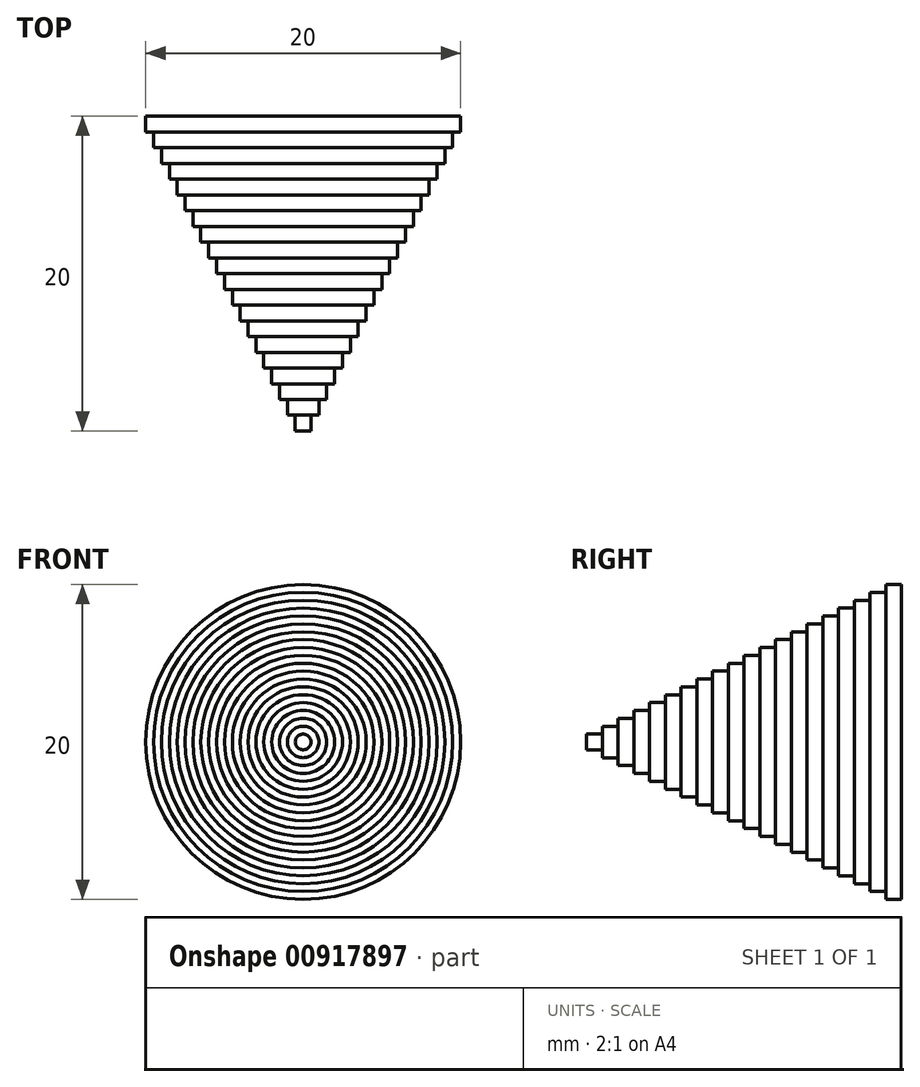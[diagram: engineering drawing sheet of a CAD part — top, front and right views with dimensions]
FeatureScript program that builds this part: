
annotation { "Feature Type Name" : "Feature", "Feature Type Description" : "" }
export const myFeature = defineFeature(function(context is Context, id is Id, definition is map)
    precondition{}
    {
        {
            var Q0;
            Q0=qCreatedBy(makeId("Front.planeOp"),FACE);
            var sketch = newSketch(context, id + "F0", { "sketchPlane" : qUnion([Q0])});
            skCircle(sketch, "E0", {"center": v(0, 10.2) * mm, "radius": 10 * mm});
            skSolve(sketch);
        }
        {
            var Q0;
            Q0=makeQuery(id+"F0.imprint","IMPRINT",FACE,{"disambiguationData":[TD([[makeQuery(id+"F0.imprint","IMPRINT",EDGE,{"derivedFrom":sQuery(id+"F0.wireOp",EDGE,"E0")}),1.0]])]});
            extrude(context, id + "F1", {"entities" : qUnion([Q0]), "depth" : 1 * mm, "offsetDistance" : 25 * mm});
        }
        {
            var Q0;
            Q0=makeQuery(id+"F1.opExtrude","CAP_FACE",FACE,{"disambiguationData":[OSD([sQuery(id+"F0.wireOp",EDGE,"E0")])],"isStart":false});
            var sketch = newSketch(context, id + "F2", { "sketchPlane" : qUnion([Q0])});
            skCircle(sketch, "E1", {"center": v(0, 10.2) * mm, "radius": 9.5 * mm});
            skSolve(sketch);
        }
        {
            var Q0;
            Q0=makeQuery(id+"F2.imprint","IMPRINT",FACE,{"disambiguationData":[TD([[makeQuery(id+"F2.imprint","IMPRINT",EDGE,{"derivedFrom":sQuery(id+"F2.wireOp",EDGE,"E1")}),1.0]])]});
            extrude(context, id + "F3", {"entities" : qUnion([Q0]), "operationType" : NewBodyOperationType.ADD, "depth" : 1 * mm, "offsetDistance" : 25 * mm});
        }
        {
            var Q0;
            Q0=makeQuery(id+"F3.opExtrude","CAP_FACE",FACE,{"disambiguationData":[OSD([sQuery(id+"F2.wireOp",EDGE,"E1")])],"isStart":false});
            var sketch = newSketch(context, id + "F4", { "sketchPlane" : qUnion([Q0])});
            skCircle(sketch, "E2", {"center": v(0, 10.2) * mm, "radius": 9 * mm});
            skSolve(sketch);
        }
        {
            var Q0;
            Q0=makeQuery(id+"F4.imprint","IMPRINT",FACE,{"disambiguationData":[TD([[makeQuery(id+"F4.imprint","IMPRINT",EDGE,{"derivedFrom":sQuery(id+"F4.wireOp",EDGE,"E2")}),1.0]])]});
            extrude(context, id + "F5", {"entities" : qUnion([Q0]), "operationType" : NewBodyOperationType.ADD, "depth" : 1 * mm, "offsetDistance" : 25 * mm});
        }
        {
            var Q0;
            Q0=makeQuery(id+"F5.opExtrude","CAP_FACE",FACE,{"disambiguationData":[OSD([sQuery(id+"F4.wireOp",EDGE,"E2")])],"isStart":false});
            var sketch = newSketch(context, id + "F6", { "sketchPlane" : qUnion([Q0])});
            skCircle(sketch, "E3", {"center": v(0, 10.2) * mm, "radius": 8.5 * mm});
            skSolve(sketch);
        }
        {
            var Q0;
            Q0=makeQuery(id+"F6.imprint","IMPRINT",FACE,{"disambiguationData":[TD([[makeQuery(id+"F6.imprint","IMPRINT",EDGE,{"derivedFrom":sQuery(id+"F6.wireOp",EDGE,"E3")}),1.0]])]});
            extrude(context, id + "F7", {"entities" : qUnion([Q0]), "operationType" : NewBodyOperationType.ADD, "depth" : 1 * mm, "offsetDistance" : 25 * mm});
        }
        {
            var Q0;
            Q0=makeQuery(id+"F7.opExtrude","CAP_FACE",FACE,{"disambiguationData":[OSD([sQuery(id+"F6.wireOp",EDGE,"E3")])],"isStart":false});
            var sketch = newSketch(context, id + "F8", { "sketchPlane" : qUnion([Q0])});
            skCircle(sketch, "E4", {"center": v(0, 10.2) * mm, "radius": 8 * mm});
            skSolve(sketch);
        }
        {
            var Q0;
            Q0=makeQuery(id+"F8.imprint","IMPRINT",FACE,{"disambiguationData":[TD([[makeQuery(id+"F8.imprint","IMPRINT",EDGE,{"derivedFrom":sQuery(id+"F8.wireOp",EDGE,"E4")}),1.0]])]});
            extrude(context, id + "F9", {"entities" : qUnion([Q0]), "operationType" : NewBodyOperationType.ADD, "depth" : 1 * mm, "offsetDistance" : 25 * mm});
        }
        {
            var Q0;
            Q0=makeQuery(id+"F9.opExtrude","CAP_FACE",FACE,{"disambiguationData":[OSD([sQuery(id+"F8.wireOp",EDGE,"E4")])],"isStart":false});
            var sketch = newSketch(context, id + "F10", { "sketchPlane" : qUnion([Q0])});
            skCircle(sketch, "E5", {"center": v(0, 10.2) * mm, "radius": 7.5 * mm});
            skSolve(sketch);
        }
        {
            var Q0;
            Q0=makeQuery(id+"F10.imprint","IMPRINT",FACE,{"disambiguationData":[TD([[makeQuery(id+"F10.imprint","IMPRINT",EDGE,{"derivedFrom":sQuery(id+"F10.wireOp",EDGE,"E5")}),1.0]])]});
            extrude(context, id + "F11", {"entities" : qUnion([Q0]), "operationType" : NewBodyOperationType.ADD, "depth" : 1 * mm, "offsetDistance" : 25 * mm});
        }
        {
            var Q0;
            Q0=makeQuery(id+"F11.opExtrude","CAP_FACE",FACE,{"disambiguationData":[OSD([sQuery(id+"F10.wireOp",EDGE,"E5")])],"isStart":false});
            var sketch = newSketch(context, id + "F12", { "sketchPlane" : qUnion([Q0])});
            skCircle(sketch, "E6", {"center": v(0, 10.2) * mm, "radius": 7 * mm});
            skSolve(sketch);
        }
        {
            var Q0;
            Q0=makeQuery(id+"F12.imprint","IMPRINT",FACE,{"disambiguationData":[TD([[makeQuery(id+"F12.imprint","IMPRINT",EDGE,{"derivedFrom":sQuery(id+"F12.wireOp",EDGE,"E6")}),1.0]])]});
            extrude(context, id + "F13", {"entities" : qUnion([Q0]), "operationType" : NewBodyOperationType.ADD, "depth" : 1 * mm, "offsetDistance" : 25 * mm});
        }
        {
            var Q0;
            Q0=makeQuery(id+"F13.opExtrude","CAP_FACE",FACE,{"disambiguationData":[OSD([sQuery(id+"F12.wireOp",EDGE,"E6")])],"isStart":false});
            var sketch = newSketch(context, id + "F14", { "sketchPlane" : qUnion([Q0])});
            skCircle(sketch, "E7", {"center": v(0, 10.2) * mm, "radius": 6.5 * mm});
            skSolve(sketch);
        }
        {
            var Q0;
            Q0=makeQuery(id+"F14.imprint","IMPRINT",FACE,{"disambiguationData":[TD([[makeQuery(id+"F14.imprint","IMPRINT",EDGE,{"derivedFrom":sQuery(id+"F14.wireOp",EDGE,"E7")}),1.0]])]});
            extrude(context, id + "F15", {"entities" : qUnion([Q0]), "operationType" : NewBodyOperationType.ADD, "depth" : 1 * mm, "offsetDistance" : 25 * mm});
        }
        {
            var Q0;
            Q0=makeQuery(id+"F15.opExtrude","CAP_FACE",FACE,{"disambiguationData":[OSD([sQuery(id+"F14.wireOp",EDGE,"E7")])],"isStart":false});
            var sketch = newSketch(context, id + "F16", { "sketchPlane" : qUnion([Q0])});
            skCircle(sketch, "E8", {"center": v(0, 10.2) * mm, "radius": 6 * mm});
            skSolve(sketch);
        }
        {
            var Q0;
            Q0=makeQuery(id+"F16.imprint","IMPRINT",FACE,{"disambiguationData":[TD([[makeQuery(id+"F16.imprint","IMPRINT",EDGE,{"derivedFrom":sQuery(id+"F16.wireOp",EDGE,"E8")}),1.0]])]});
            extrude(context, id + "F17", {"entities" : qUnion([Q0]), "operationType" : NewBodyOperationType.ADD, "depth" : 1 * mm, "offsetDistance" : 25 * mm});
        }
        {
            var Q0;
            Q0=makeQuery(id+"F17.opExtrude","CAP_FACE",FACE,{"disambiguationData":[OSD([sQuery(id+"F16.wireOp",EDGE,"E8")])],"isStart":false});
            var sketch = newSketch(context, id + "F18", { "sketchPlane" : qUnion([Q0])});
            skCircle(sketch, "E9", {"center": v(0, 10.2) * mm, "radius": 5.5 * mm});
            skSolve(sketch);
        }
        {
            var Q0;
            Q0=makeQuery(id+"F18.imprint","IMPRINT",FACE,{"disambiguationData":[TD([[makeQuery(id+"F18.imprint","IMPRINT",EDGE,{"derivedFrom":sQuery(id+"F18.wireOp",EDGE,"E9")}),1.0]])]});
            extrude(context, id + "F19", {"entities" : qUnion([Q0]), "operationType" : NewBodyOperationType.ADD, "depth" : 1 * mm, "offsetDistance" : 25 * mm});
        }
        {
            var Q0;
            Q0=makeQuery(id+"F19.opExtrude","CAP_FACE",FACE,{"disambiguationData":[OSD([sQuery(id+"F18.wireOp",EDGE,"E9")])],"isStart":false});
            var sketch = newSketch(context, id + "F20", { "sketchPlane" : qUnion([Q0])});
            skCircle(sketch, "E10", {"center": v(0, 10.2) * mm, "radius": 5 * mm});
            skSolve(sketch);
        }
        {
            var Q0;
            Q0=makeQuery(id+"F20.imprint","IMPRINT",FACE,{"disambiguationData":[TD([[makeQuery(id+"F20.imprint","IMPRINT",EDGE,{"derivedFrom":sQuery(id+"F20.wireOp",EDGE,"E10")}),1.0]])]});
            extrude(context, id + "F21", {"entities" : qUnion([Q0]), "operationType" : NewBodyOperationType.ADD, "depth" : 1 * mm, "offsetDistance" : 25 * mm});
        }
        {
            var Q0;
            Q0=makeQuery(id+"F21.opExtrude","CAP_FACE",FACE,{"disambiguationData":[OSD([sQuery(id+"F20.wireOp",EDGE,"E10")])],"isStart":false});
            var sketch = newSketch(context, id + "F22", { "sketchPlane" : qUnion([Q0])});
            skCircle(sketch, "E11", {"center": v(0, 10.2) * mm, "radius": 4.5 * mm});
            skSolve(sketch);
        }
        {
            var Q0;
            Q0=makeQuery(id+"F22.imprint","IMPRINT",FACE,{"disambiguationData":[TD([[makeQuery(id+"F22.imprint","IMPRINT",EDGE,{"derivedFrom":sQuery(id+"F22.wireOp",EDGE,"E11")}),1.0]])]});
            extrude(context, id + "F23", {"entities" : qUnion([Q0]), "operationType" : NewBodyOperationType.ADD, "depth" : 1 * mm, "offsetDistance" : 25 * mm});
        }
        {
            var Q0;
            Q0=makeQuery(id+"F23.opExtrude","CAP_FACE",FACE,{"disambiguationData":[OSD([sQuery(id+"F22.wireOp",EDGE,"E11")])],"isStart":false});
            var sketch = newSketch(context, id + "F24", { "sketchPlane" : qUnion([Q0])});
            skCircle(sketch, "E12", {"center": v(0, 10.2) * mm, "radius": 4 * mm});
            skSolve(sketch);
        }
        {
            var Q0;
            Q0=makeQuery(id+"F24.imprint","IMPRINT",FACE,{"disambiguationData":[TD([[makeQuery(id+"F24.imprint","IMPRINT",EDGE,{"derivedFrom":sQuery(id+"F24.wireOp",EDGE,"E12")}),1.0]])]});
            extrude(context, id + "F25", {"entities" : qUnion([Q0]), "operationType" : NewBodyOperationType.ADD, "depth" : 1 * mm, "offsetDistance" : 25 * mm});
        }
        {
            var Q0;
            Q0=makeQuery(id+"F25.opExtrude","CAP_FACE",FACE,{"disambiguationData":[OSD([sQuery(id+"F24.wireOp",EDGE,"E12")])],"isStart":false});
            var sketch = newSketch(context, id + "F26", { "sketchPlane" : qUnion([Q0])});
            skCircle(sketch, "E13", {"center": v(0, 10.2) * mm, "radius": 3.5 * mm});
            skSolve(sketch);
        }
        {
            var Q0;
            Q0=makeQuery(id+"F26.imprint","IMPRINT",FACE,{"disambiguationData":[TD([[makeQuery(id+"F26.imprint","IMPRINT",EDGE,{"derivedFrom":sQuery(id+"F26.wireOp",EDGE,"E13")}),1.0]])]});
            extrude(context, id + "F27", {"entities" : qUnion([Q0]), "operationType" : NewBodyOperationType.ADD, "depth" : 1 * mm, "offsetDistance" : 25 * mm});
        }
        {
            var Q0;
            Q0=makeQuery(id+"F27.opExtrude","CAP_FACE",FACE,{"disambiguationData":[OSD([sQuery(id+"F26.wireOp",EDGE,"E13")])],"isStart":false});
            var sketch = newSketch(context, id + "F28", { "sketchPlane" : qUnion([Q0])});
            skCircle(sketch, "E14", {"center": v(0, 10.2) * mm, "radius": 3 * mm});
            skSolve(sketch);
        }
        {
            var Q0;
            Q0=makeQuery(id+"F28.imprint","IMPRINT",FACE,{"disambiguationData":[TD([[makeQuery(id+"F28.imprint","IMPRINT",EDGE,{"derivedFrom":sQuery(id+"F28.wireOp",EDGE,"E14")}),1.0]])]});
            extrude(context, id + "F29", {"entities" : qUnion([Q0]), "operationType" : NewBodyOperationType.ADD, "depth" : 1 * mm, "offsetDistance" : 25 * mm});
        }
        {
            var Q0;
            Q0=makeQuery(id+"F29.opExtrude","CAP_FACE",FACE,{"disambiguationData":[OSD([sQuery(id+"F28.wireOp",EDGE,"E14")])],"isStart":false});
            var sketch = newSketch(context, id + "F30", { "sketchPlane" : qUnion([Q0])});
            skCircle(sketch, "E15", {"center": v(0, 10.2) * mm, "radius": 2.5 * mm});
            skSolve(sketch);
        }
        {
            var Q0;
            Q0=makeQuery(id+"F30.imprint","IMPRINT",FACE,{"disambiguationData":[TD([[makeQuery(id+"F30.imprint","IMPRINT",EDGE,{"derivedFrom":sQuery(id+"F30.wireOp",EDGE,"E15")}),1.0]])]});
            extrude(context, id + "F31", {"entities" : qUnion([Q0]), "operationType" : NewBodyOperationType.ADD, "depth" : 1 * mm, "offsetDistance" : 25 * mm});
        }
        {
            var Q0;
            Q0=makeQuery(id+"F31.opExtrude","CAP_FACE",FACE,{"disambiguationData":[OSD([sQuery(id+"F30.wireOp",EDGE,"E15")])],"isStart":false});
            var sketch = newSketch(context, id + "F32", { "sketchPlane" : qUnion([Q0])});
            skCircle(sketch, "E16", {"center": v(0, 10.2) * mm, "radius": 2 * mm});
            skSolve(sketch);
        }
        {
            var Q0;
            Q0=makeQuery(id+"F32.imprint","IMPRINT",FACE,{"disambiguationData":[TD([[makeQuery(id+"F32.imprint","IMPRINT",EDGE,{"derivedFrom":sQuery(id+"F32.wireOp",EDGE,"E16")}),1.0]])]});
            extrude(context, id + "F33", {"entities" : qUnion([Q0]), "operationType" : NewBodyOperationType.ADD, "depth" : 1 * mm, "offsetDistance" : 25 * mm});
        }
        {
            var Q0;
            Q0=makeQuery(id+"F33.opExtrude","CAP_FACE",FACE,{"disambiguationData":[OSD([sQuery(id+"F32.wireOp",EDGE,"E16")])],"isStart":false});
            var sketch = newSketch(context, id + "F34", { "sketchPlane" : qUnion([Q0])});
            skCircle(sketch, "E17", {"center": v(0, 10.2) * mm, "radius": 1.5 * mm});
            skSolve(sketch);
        }
        {
            var Q0;
            Q0=makeQuery(id+"F34.imprint","IMPRINT",FACE,{"disambiguationData":[TD([[makeQuery(id+"F34.imprint","IMPRINT",EDGE,{"derivedFrom":sQuery(id+"F34.wireOp",EDGE,"E17")}),1.0]])]});
            extrude(context, id + "F35", {"entities" : qUnion([Q0]), "operationType" : NewBodyOperationType.ADD, "depth" : 1 * mm, "offsetDistance" : 25 * mm});
        }
        {
            var Q0;
            Q0=makeQuery(id+"F35.opExtrude","CAP_FACE",FACE,{"disambiguationData":[OSD([sQuery(id+"F34.wireOp",EDGE,"E17")])],"isStart":false});
            var sketch = newSketch(context, id + "F36", { "sketchPlane" : qUnion([Q0])});
            skCircle(sketch, "E18", {"center": v(0, 10.2) * mm, "radius": 1 * mm});
            skSolve(sketch);
        }
        {
            var Q0;
            Q0=makeQuery(id+"F36.imprint","IMPRINT",FACE,{"disambiguationData":[TD([[makeQuery(id+"F36.imprint","IMPRINT",EDGE,{"derivedFrom":sQuery(id+"F36.wireOp",EDGE,"E18")}),1.0]])]});
            extrude(context, id + "F37", {"entities" : qUnion([Q0]), "operationType" : NewBodyOperationType.ADD, "depth" : 1 * mm, "offsetDistance" : 25 * mm});
        }
        {
            var Q0;
            Q0=makeQuery(id+"F37.opExtrude","CAP_FACE",FACE,{"disambiguationData":[OSD([sQuery(id+"F36.wireOp",EDGE,"E18")])],"isStart":false});
            var sketch = newSketch(context, id + "F38", { "sketchPlane" : qUnion([Q0])});
            skCircle(sketch, "E19", {"center": v(0, 10.2) * mm, "radius": 0.5 * mm});
            skSolve(sketch);
        }
        {
            var Q0;
            Q0=makeQuery(id+"F38.imprint","IMPRINT",FACE,{"disambiguationData":[TD([[makeQuery(id+"F38.imprint","IMPRINT",EDGE,{"derivedFrom":sQuery(id+"F38.wireOp",EDGE,"E19")}),1.0]])]});
            extrude(context, id + "F39", {"entities" : qUnion([Q0]), "operationType" : NewBodyOperationType.ADD, "depth" : 1 * mm, "offsetDistance" : 25 * mm});
        }
    });
